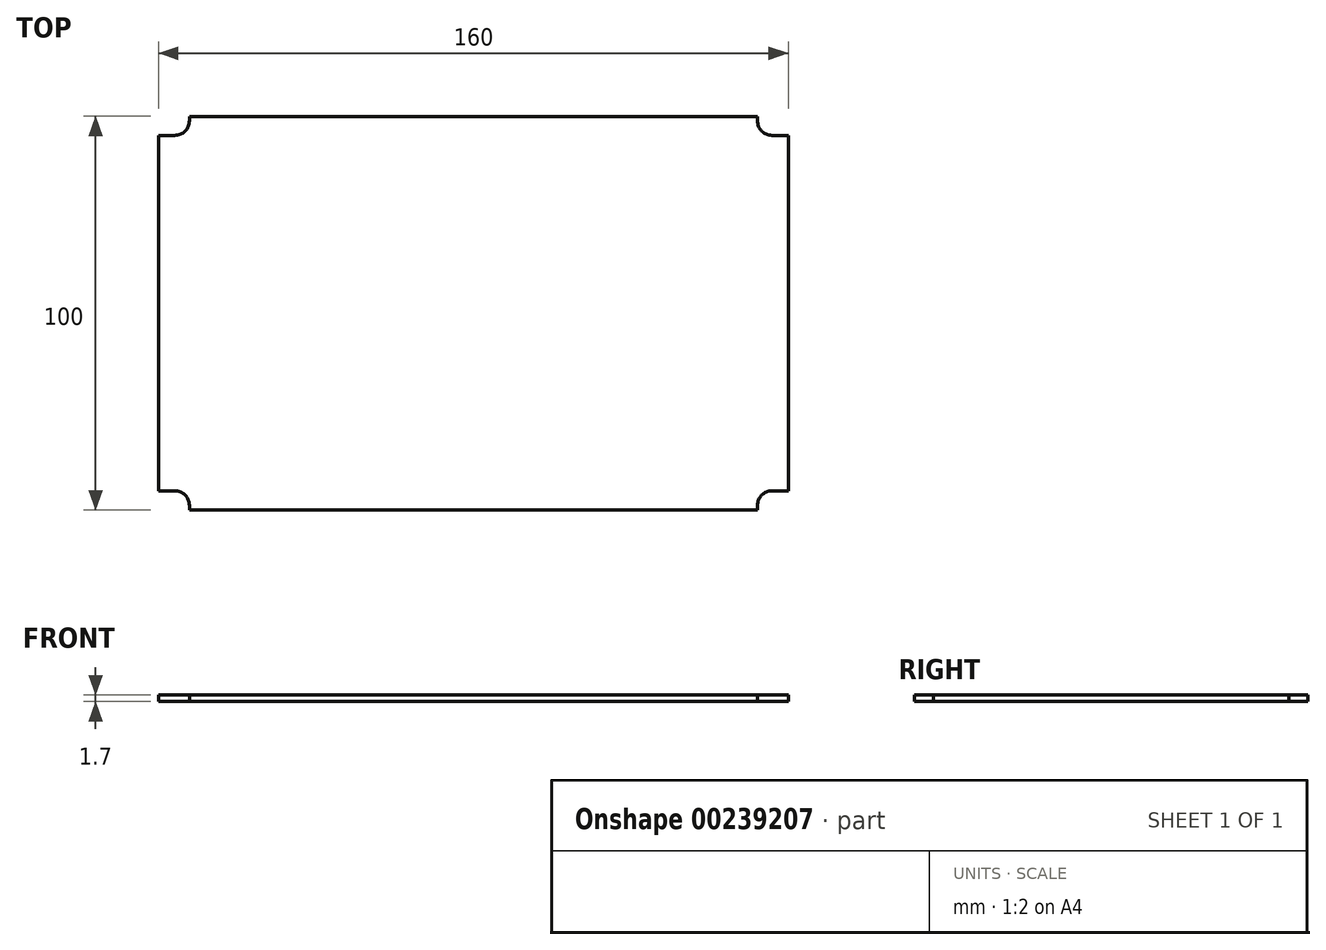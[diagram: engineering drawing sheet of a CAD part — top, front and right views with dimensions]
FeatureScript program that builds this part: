
annotation { "Feature Type Name" : "Feature", "Feature Type Description" : "" }
export const myFeature = defineFeature(function(context is Context, id is Id, definition is map)
    precondition{}
    {
        {
            var Q0;
            Q0=qCreatedBy(makeId("Top.planeOp"),FACE);
            var sketch = newSketch(context, id + "F0", { "sketchPlane" : qUnion([Q0])});
            skLineSegment(sketch, "E0.bottom", {"start": v(-72.18, -50) * mm, "end": v(72.15, -50) * mm});
            skLineSegment(sketch, "E0.top", {"start": v(-72.18, 50) * mm, "end": v(72.15, 50) * mm});
            skLineSegment(sketch, "E0.left", {"start": v(-80.02, -45.16) * mm, "end": v(-80.02, 45.17) * mm});
            skLineSegment(sketch, "E0.right", {"start": v(79.98, -45.16) * mm, "end": v(79.98, 45.17) * mm});
            skLineSegment(sketch, "E1.top", {"start": v(79.98, 45.17) * mm, "end": v(75.85, 45.17) * mm});
            skLineSegment(sketch, "E1.right", {"start": v(72.15, 50) * mm, "end": v(72.15, 48.87) * mm});
            skLineSegment(sketch, "E2.top", {"start": v(79.98, -45.16) * mm, "end": v(75.85, -45.16) * mm});
            skLineSegment(sketch, "E2.right", {"start": v(72.15, -50) * mm, "end": v(72.15, -48.86) * mm});
            skLineSegment(sketch, "E3.top", {"start": v(-80.02, -45.16) * mm, "end": v(-75.88, -45.16) * mm});
            skLineSegment(sketch, "E3.right", {"start": v(-72.18, -50) * mm, "end": v(-72.18, -48.86) * mm});
            skLineSegment(sketch, "E4.top", {"start": v(-80.02, 45.17) * mm, "end": v(-75.88, 45.17) * mm});
            skLineSegment(sketch, "E4.right", {"start": v(-72.18, 50) * mm, "end": v(-72.18, 48.87) * mm});
            skPoint(sketch, "E5.visualSharp", {"position": v(-72.18, 45.17) * mm});
            skArc(sketch, "E5.filletArc", {"start": v(-75.88, 45.17) * mm, "mid": v(-73.26, 46.25) * mm, "end": v(-72.18, 48.87) * mm});
            skPoint(sketch, "E6.visualSharp", {"position": v(72.15, 45.17) * mm});
            skArc(sketch, "E6.filletArc", {"start": v(72.15, 48.87) * mm, "mid": v(73.23, 46.25) * mm, "end": v(75.85, 45.17) * mm});
            skPoint(sketch, "E7.visualSharp", {"position": v(72.15, -45.16) * mm});
            skArc(sketch, "E7.filletArc", {"start": v(75.85, -45.16) * mm, "mid": v(73.23, -46.24) * mm, "end": v(72.15, -48.86) * mm});
            skPoint(sketch, "E8.visualSharp", {"position": v(-72.18, -45.16) * mm});
            skArc(sketch, "E8.filletArc", {"start": v(-72.18, -48.86) * mm, "mid": v(-73.26, -46.24) * mm, "end": v(-75.88, -45.16) * mm});
            skLineSegment(sketch, "E9", {"start": v(0, 50) * mm, "end": v(0, 101.17) * mm});
            skLineSegment(sketch, "E10", {"start": v(-80.02, 0) * mm, "end": v(-142.31, 0) * mm});
            skSolve(sketch);
        }
        {
            var Q0;
            Q0=makeQuery(id+"F0.imprint","IMPRINT",FACE,{"disambiguationData":[TD([[makeQuery(id+"F0.imprint","IMPRINT",EDGE,{"derivedFrom":sQuery(id+"F0.wireOp",EDGE,"E0.bottom")}),1.0]])]});
            extrude(context, id + "F1", {"entities" : qUnion([Q0]), "depth" : 1.7 * mm});
        }
    });
